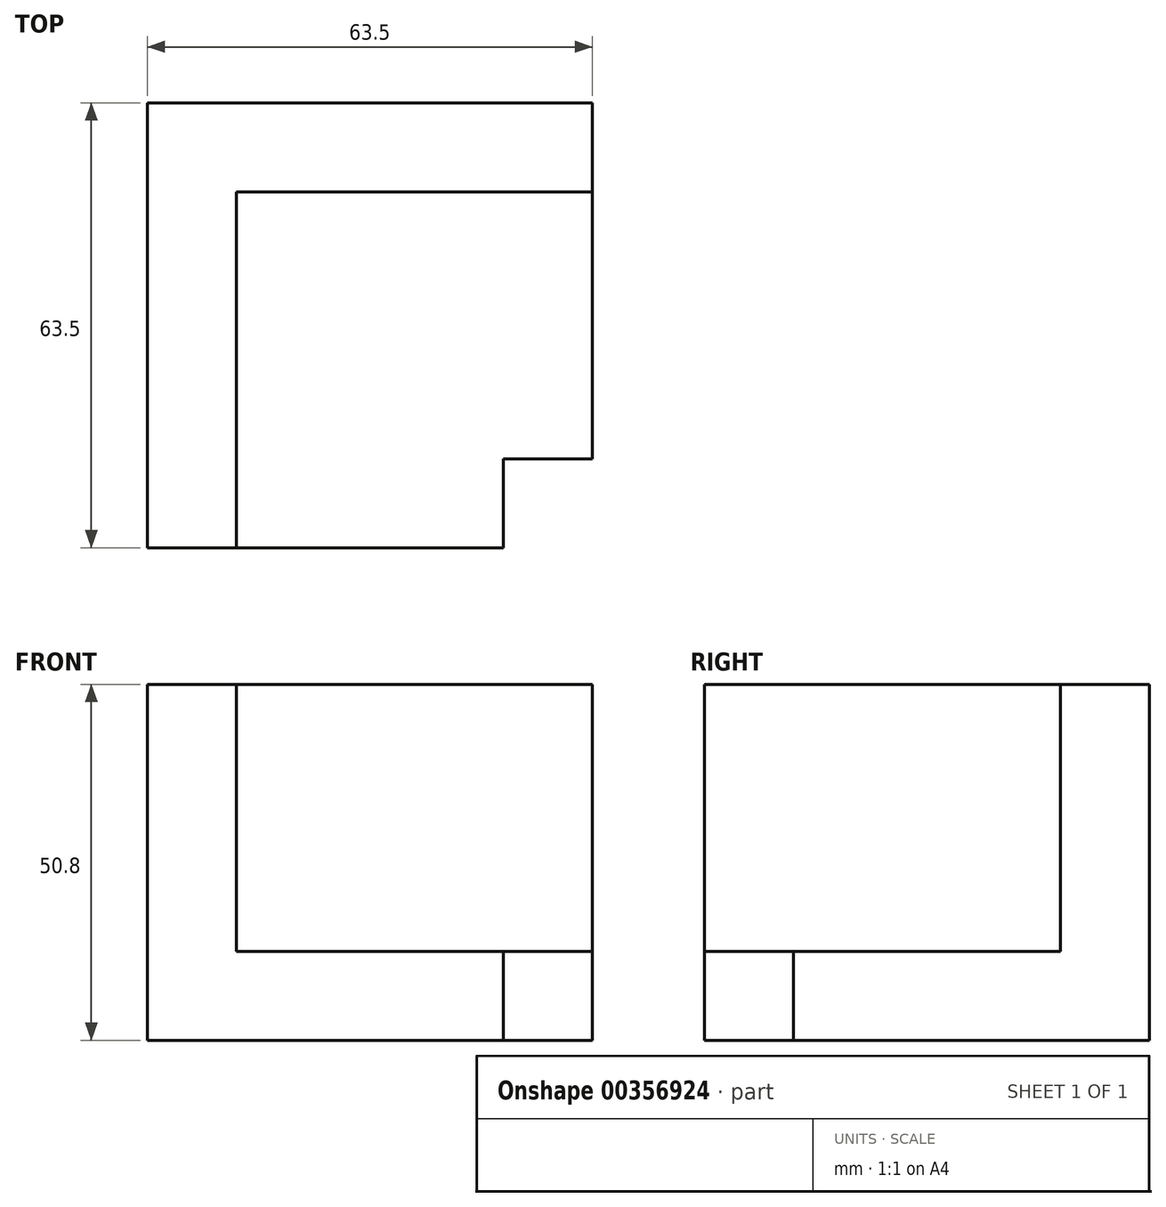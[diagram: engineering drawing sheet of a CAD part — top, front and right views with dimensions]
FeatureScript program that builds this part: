
annotation { "Feature Type Name" : "Feature", "Feature Type Description" : "" }
export const myFeature = defineFeature(function(context is Context, id is Id, definition is map)
    precondition{}
    {
        {
            var Q0;
            Q0=qCreatedBy(makeId("Front.planeOp"),FACE);
            var sketch = newSketch(context, id + "F0", { "sketchPlane" : qUnion([Q0])});
            skLineSegment(sketch, "E0.bottom", {"start": v(0, 0) * mm, "end": v(12.7, 0) * mm});
            skLineSegment(sketch, "E0.top", {"start": v(0, -50.8) * mm, "end": v(12.7, -50.8) * mm});
            skLineSegment(sketch, "E0.left", {"start": v(0, 0) * mm, "end": v(0, -50.8) * mm});
            skLineSegment(sketch, "E0.right", {"start": v(12.7, 0) * mm, "end": v(12.7, -50.8) * mm});
            skSolve(sketch);
        }
        {
            var Q0;
            Q0=makeQuery(id+"F0.imprint","IMPRINT",FACE,{"disambiguationData":[TD([[makeQuery(id+"F0.imprint","IMPRINT",EDGE,{"derivedFrom":sQuery(id+"F0.wireOp",EDGE,"E0.bottom")}),-1.0]])]});
            extrude(context, id + "F1", {"entities" : qUnion([Q0]), "depth" : 63.5 * mm});
        }
        {
            var Q0;
            Q0=makeQuery(id+"F1.opExtrude","SWEPT_FACE",FACE,{"disambiguationData":[OSD([sQuery(id+"F0.wireOp",EDGE,"E0.right")])]});
            var sketch = newSketch(context, id + "F2", { "sketchPlane" : qUnion([Q0])});
            skLineSegment(sketch, "E1.bottom", {"start": v(-63.5, -50.8) * mm, "end": v(0, -50.8) * mm});
            skLineSegment(sketch, "E1.top", {"start": v(-63.5, -38.1) * mm, "end": v(0, -38.1) * mm});
            skLineSegment(sketch, "E1.left", {"start": v(-63.5, -50.8) * mm, "end": v(-63.5, -38.1) * mm});
            skLineSegment(sketch, "E1.right", {"start": v(0, -50.8) * mm, "end": v(0, -38.1) * mm});
            skSolve(sketch);
        }
        {
            var Q0;
            Q0=makeQuery(id+"F2.imprint","IMPRINT",FACE,{"disambiguationData":[TD([[makeQuery(id+"F2.imprint","IMPRINT",EDGE,{"derivedFrom":sQuery(id+"F2.wireOp",EDGE,"E1.bottom")}),1.0]])]});
            extrude(context, id + "F3", {"entities" : qUnion([Q0]), "operationType" : NewBodyOperationType.ADD, "depth" : 50.8 * mm});
        }
        {
            var Q0;
            Q0=makeQuery(id+"F1.opExtrude","SWEPT_FACE",FACE,{"disambiguationData":[OSD([sQuery(id+"F0.wireOp",EDGE,"E0.right")])]});
            var sketch = newSketch(context, id + "F4", { "sketchPlane" : qUnion([Q0])});
            skLineSegment(sketch, "E2.bottom", {"start": v(0, 0) * mm, "end": v(-12.7, 0) * mm});
            skLineSegment(sketch, "E2.top", {"start": v(0, -38.1) * mm, "end": v(-12.7, -38.1) * mm});
            skLineSegment(sketch, "E2.left", {"start": v(0, 0) * mm, "end": v(0, -38.1) * mm});
            skLineSegment(sketch, "E2.right", {"start": v(-12.7, 0) * mm, "end": v(-12.7, -38.1) * mm});
            skSolve(sketch);
        }
        {
            var Q0;
            Q0=makeQuery(id+"F4.imprint","IMPRINT",FACE,{"disambiguationData":[TD([[makeQuery(id+"F4.imprint","IMPRINT",EDGE,{"derivedFrom":sQuery(id+"F4.wireOp",EDGE,"E2.bottom")}),-1.0]])]});
            extrude(context, id + "F5", {"entities" : qUnion([Q0]), "operationType" : NewBodyOperationType.ADD, "depth" : 50.8 * mm});
        }
        {
            var Q0;
            Q0=makeQuery(id+"F5.boolean.opBoolean","MERGE",FACE,{"derivedFrom":[makeQuery(id+"F3.opExtrude","CAP_FACE",FACE,{"disambiguationData":[OSD([sQuery(id+"F2.wireOp",EDGE,"E1.bottom"),sQuery(id+"F2.wireOp",EDGE,"E1.top"),sQuery(id+"F2.wireOp",EDGE,"E1.left"),sQuery(id+"F2.wireOp",EDGE,"E1.right")])],"isStart":false}),makeQuery(id+"F5.opExtrude","CAP_FACE",FACE,{"disambiguationData":[OSD([sQuery(id+"F4.wireOp",EDGE,"E2.bottom"),sQuery(id+"F4.wireOp",EDGE,"E2.top"),sQuery(id+"F4.wireOp",EDGE,"E2.left"),sQuery(id+"F4.wireOp",EDGE,"E2.right")])],"isStart":false})]});
            var sketch = newSketch(context, id + "F6", { "sketchPlane" : qUnion([Q0])});
            skLineSegment(sketch, "E3.bottom", {"start": v(-63.5, -38.1) * mm, "end": v(-50.8, -38.1) * mm});
            skLineSegment(sketch, "E3.top", {"start": v(-63.5, -50.8) * mm, "end": v(-50.8, -50.8) * mm});
            skLineSegment(sketch, "E3.left", {"start": v(-63.5, -38.1) * mm, "end": v(-63.5, -50.8) * mm});
            skLineSegment(sketch, "E3.right", {"start": v(-50.8, -38.1) * mm, "end": v(-50.8, -50.8) * mm});
            skSolve(sketch);
        }
        {
            var Q0;
            Q0=makeQuery(id+"F6.imprint","IMPRINT",FACE,{"disambiguationData":[TD([[makeQuery(id+"F6.imprint","IMPRINT",EDGE,{"derivedFrom":sQuery(id+"F6.wireOp",EDGE,"E3.bottom")}),-1.0]])]});
            extrude(context, id + "F7", {"entities" : qUnion([Q0]), "operationType" : NewBodyOperationType.ADD, "depth" : -12.7 * mm});
        }
        {
            var Q0;
            Q0=makeQuery(id+"F3.opExtrude","SWEPT_FACE",FACE,{"disambiguationData":[OSD([sQuery(id+"F2.wireOp",EDGE,"E1.top")])]});
            var sketch = newSketch(context, id + "F8", { "sketchPlane" : qUnion([Q0])});
            skLineSegment(sketch, "E4.bottom", {"start": v(63.5, -63.5) * mm, "end": v(50.8, -63.5) * mm});
            skLineSegment(sketch, "E4.top", {"start": v(63.5, -50.8) * mm, "end": v(50.8, -50.8) * mm});
            skLineSegment(sketch, "E4.left", {"start": v(63.5, -63.5) * mm, "end": v(63.5, -50.8) * mm});
            skLineSegment(sketch, "E4.right", {"start": v(50.8, -63.5) * mm, "end": v(50.8, -50.8) * mm});
            skSolve(sketch);
        }
        {
            var Q0;
            Q0=makeQuery(id+"F8.imprint","IMPRINT",FACE,{"disambiguationData":[TD([[makeQuery(id+"F8.imprint","IMPRINT",EDGE,{"derivedFrom":sQuery(id+"F8.wireOp",EDGE,"E4.bottom")}),-1.0]])]});
            extrude(context, id + "F9", {"entities" : qUnion([Q0]), "operationType" : NewBodyOperationType.REMOVE, "depth" : -12.7 * mm});
        }
        {
            var Q0;
            Q0=makeQuery(id+"F5.boolean.opBoolean","MERGE",FACE,{"derivedFrom":[makeQuery(id+"F1.opExtrude","SWEPT_FACE",FACE,{"disambiguationData":[OSD([sQuery(id+"F0.wireOp",EDGE,"E0.bottom")])]}),makeQuery(id+"F5.opExtrude","SWEPT_FACE",FACE,{"disambiguationData":[OSD([sQuery(id+"F4.wireOp",EDGE,"E2.bottom")])]})]});
            var sketch = newSketch(context, id + "F10", { "sketchPlane" : qUnion([Q0])});
            skLineSegment(sketch, "E5.bottom", {"start": v(12.7, -63.5) * mm, "end": v(0, -63.5) * mm});
            skLineSegment(sketch, "E5.top", {"start": v(12.7, 0) * mm, "end": v(0, 0) * mm});
            skLineSegment(sketch, "E5.left", {"start": v(12.7, -63.5) * mm, "end": v(12.7, 0) * mm});
            skLineSegment(sketch, "E5.right", {"start": v(0, -63.5) * mm, "end": v(0, 0) * mm});
            skSolve(sketch);
        }
        {
            var Q0;
            Q0 = qSketchRegion(id + "F10", true);
            extrude(context, id + "F11", {"entities" : qUnion([Q0]), "operationType" : NewBodyOperationType.ADD, "depth" : 12.7 * mm});
        }
        {
            var Q0;
            Q0=makeQuery(id+"F5.boolean.opBoolean","MERGE",FACE,{"derivedFrom":[makeQuery(id+"F1.opExtrude","SWEPT_FACE",FACE,{"disambiguationData":[OSD([sQuery(id+"F0.wireOp",EDGE,"E0.bottom")])]}),makeQuery(id+"F5.opExtrude","SWEPT_FACE",FACE,{"disambiguationData":[OSD([sQuery(id+"F4.wireOp",EDGE,"E2.bottom")])]})]});
            var sketch = newSketch(context, id + "F12", { "sketchPlane" : qUnion([Q0])});
            skLineSegment(sketch, "E6.bottom", {"start": v(63.5, -12.7) * mm, "end": v(12.7, -12.7) * mm});
            skLineSegment(sketch, "E6.top", {"start": v(63.5, 0) * mm, "end": v(12.7, 0) * mm});
            skLineSegment(sketch, "E6.left", {"start": v(63.5, -12.7) * mm, "end": v(63.5, 0) * mm});
            skLineSegment(sketch, "E6.right", {"start": v(12.7, -12.7) * mm, "end": v(12.7, 0) * mm});
            skSolve(sketch);
        }
        {
            var Q0;
            Q0 = qSketchRegion(id + "F12", true);
            extrude(context, id + "F13", {"entities" : qUnion([Q0]), "operationType" : NewBodyOperationType.ADD, "depth" : 12.7 * mm});
        }
        {
            var Q0;
            Q0=makeQuery(id+"F11.boolean.opBoolean","MERGE",FACE,{"derivedFrom":[makeQuery(id+"F3.boolean.opBoolean","MERGE",FACE,{"derivedFrom":[makeQuery(id+"F1.opExtrude","CAP_FACE",FACE,{"disambiguationData":[OSD([sQuery(id+"F0.wireOp",EDGE,"E0.bottom"),sQuery(id+"F0.wireOp",EDGE,"E0.top"),sQuery(id+"F0.wireOp",EDGE,"E0.left"),sQuery(id+"F0.wireOp",EDGE,"E0.right")])],"isStart":false}),makeQuery(id+"F3.opExtrude","SWEPT_FACE",FACE,{"disambiguationData":[OSD([sQuery(id+"F2.wireOp",EDGE,"E1.left")])]})]}),makeQuery(id+"F11.opExtrude","SWEPT_FACE",FACE,{"disambiguationData":[OSD([sQuery(id+"F10.wireOp",EDGE,"E5.bottom")])]})]});
            var sketch = newSketch(context, id + "F14", { "sketchPlane" : qUnion([Q0])});
            skLineSegment(sketch, "E7.bottom", {"start": v(50.8, -38.1) * mm, "end": v(0, -38.1) * mm});
            skLineSegment(sketch, "E7.top", {"start": v(50.8, -50.8) * mm, "end": v(0, -50.8) * mm});
            skLineSegment(sketch, "E7.left", {"start": v(50.8, -38.1) * mm, "end": v(50.8, -50.8) * mm});
            skLineSegment(sketch, "E7.right", {"start": v(0, -38.1) * mm, "end": v(0, -50.8) * mm});
            skLineSegment(sketch, "E8.bottom", {"start": v(12.7, 12.7) * mm, "end": v(0, 12.7) * mm});
            skLineSegment(sketch, "E8.top", {"start": v(12.7, -38.1) * mm, "end": v(0, -38.1) * mm});
            skLineSegment(sketch, "E8.left", {"start": v(12.7, 12.7) * mm, "end": v(12.7, -38.1) * mm});
            skLineSegment(sketch, "E8.right", {"start": v(0, 12.7) * mm, "end": v(0, -38.1) * mm});
            skSolve(sketch);
        }
        {
            var Q0;
            Q0 = qSketchRegion(id + "F14", true);
            extrude(context, id + "F15", {"entities" : qUnion([Q0]), "operationType" : NewBodyOperationType.ADD, "depth" : 12.7 * mm});
        }
        {
            var Q0;
            Q0=makeQuery(id+"F13.boolean.opBoolean","MERGE",FACE,{"derivedFrom":[makeQuery(id+"F5.boolean.opBoolean","MERGE",FACE,{"derivedFrom":[makeQuery(id+"F3.opExtrude","CAP_FACE",FACE,{"disambiguationData":[OSD([sQuery(id+"F2.wireOp",EDGE,"E1.bottom"),sQuery(id+"F2.wireOp",EDGE,"E1.top"),sQuery(id+"F2.wireOp",EDGE,"E1.left"),sQuery(id+"F2.wireOp",EDGE,"E1.right")])],"isStart":false}),makeQuery(id+"F5.opExtrude","CAP_FACE",FACE,{"disambiguationData":[OSD([sQuery(id+"F4.wireOp",EDGE,"E2.bottom"),sQuery(id+"F4.wireOp",EDGE,"E2.top"),sQuery(id+"F4.wireOp",EDGE,"E2.left"),sQuery(id+"F4.wireOp",EDGE,"E2.right")])],"isStart":false})]}),makeQuery(id+"F13.opExtrude","SWEPT_FACE",FACE,{"disambiguationData":[OSD([sQuery(id+"F12.wireOp",EDGE,"E6.left")])]})]});
            var sketch = newSketch(context, id + "F16", { "sketchPlane" : qUnion([Q0])});
            skLineSegment(sketch, "E9.bottom", {"start": v(-50.8, -50.8) * mm, "end": v(0, -50.8) * mm});
            skLineSegment(sketch, "E9.top", {"start": v(-50.8, -38.1) * mm, "end": v(0, -38.1) * mm});
            skLineSegment(sketch, "E9.left", {"start": v(-50.8, -50.8) * mm, "end": v(-50.8, -38.1) * mm});
            skLineSegment(sketch, "E9.right", {"start": v(0, -50.8) * mm, "end": v(0, -38.1) * mm});
            skLineSegment(sketch, "E10.bottom", {"start": v(-12.7, 12.7) * mm, "end": v(0, 12.7) * mm});
            skLineSegment(sketch, "E10.top", {"start": v(-12.7, -38.1) * mm, "end": v(0, -38.1) * mm});
            skLineSegment(sketch, "E10.left", {"start": v(-12.7, 12.7) * mm, "end": v(-12.7, -38.1) * mm});
            skLineSegment(sketch, "E10.right", {"start": v(0, 12.7) * mm, "end": v(0, -38.1) * mm});
            skSolve(sketch);
        }
        {
            var Q0;
            Q0 = qSketchRegion(id + "F16", true);
            extrude(context, id + "F17", {"entities" : qUnion([Q0]), "operationType" : NewBodyOperationType.ADD, "depth" : 12.7 * mm});
        }
        {
            var Q0;
            Q0=makeQuery(id+"F15.boolean.opBoolean","MERGE",FACE,{"derivedFrom":[makeQuery(id+"F9.boolean.opBoolean","COPY",FACE,{"derivedFrom":makeQuery(id+"F9.opExtrude","SWEPT_FACE",FACE,{"disambiguationData":[OSD([sQuery(id+"F8.wireOp",EDGE,"E4.right")])]})}),makeQuery(id+"F15.opExtrude","SWEPT_FACE",FACE,{"disambiguationData":[OSD([sQuery(id+"F14.wireOp",EDGE,"E7.left")])]})]});
            var sketch = newSketch(context, id + "F18", { "sketchPlane" : qUnion([Q0])});
            skLineSegment(sketch, "E11.bottom", {"start": v(-50.8, -38.1) * mm, "end": v(-63.5, -38.1) * mm});
            skLineSegment(sketch, "E11.top", {"start": v(-50.8, -50.8) * mm, "end": v(-63.5, -50.8) * mm});
            skLineSegment(sketch, "E11.left", {"start": v(-50.8, -38.1) * mm, "end": v(-50.8, -50.8) * mm});
            skLineSegment(sketch, "E11.right", {"start": v(-63.5, -38.1) * mm, "end": v(-63.5, -50.8) * mm});
            skSolve(sketch);
        }
        {
            var Q0;
            Q0 = qSketchRegion(id + "F18", true);
            extrude(context, id + "F19", {"entities" : qUnion([Q0]), "operationType" : NewBodyOperationType.ADD, "depth" : 25.4 * mm});
        }
        {
            var Q0;
            Q0=makeQuery(id+"F15.boolean.opBoolean","MERGE",FACE,{"derivedFrom":[makeQuery(id+"F9.boolean.opBoolean","COPY",FACE,{"derivedFrom":makeQuery(id+"F9.opExtrude","SWEPT_FACE",FACE,{"disambiguationData":[OSD([sQuery(id+"F8.wireOp",EDGE,"E4.right")])]})}),makeQuery(id+"F15.opExtrude","SWEPT_FACE",FACE,{"disambiguationData":[OSD([sQuery(id+"F14.wireOp",EDGE,"E7.left")])]})]});
            var sketch = newSketch(context, id + "F20", { "sketchPlane" : qUnion([Q0])});
            skLineSegment(sketch, "E12.bottom", {"start": v(-76.2, -38.1) * mm, "end": v(-63.5, -38.1) * mm});
            skLineSegment(sketch, "E12.top", {"start": v(-76.2, -50.8) * mm, "end": v(-63.5, -50.8) * mm});
            skLineSegment(sketch, "E12.left", {"start": v(-76.2, -38.1) * mm, "end": v(-76.2, -50.8) * mm});
            skLineSegment(sketch, "E12.right", {"start": v(-63.5, -38.1) * mm, "end": v(-63.5, -50.8) * mm});
            skSolve(sketch);
        }
        {
            var Q0;
            Q0 = qSketchRegion(id + "F20", true);
            extrude(context, id + "F21", {"entities" : qUnion([Q0]), "operationType" : NewBodyOperationType.ADD, "depth" : 12.7 * mm});
        }
        {
            var Q0;
            Q0=makeQuery(id+"F17.boolean.opBoolean","MERGE",FACE,{"derivedFrom":[makeQuery(id+"F15.boolean.opBoolean","MERGE",FACE,{"derivedFrom":[makeQuery(id+"F13.boolean.opBoolean","MERGE",FACE,{"derivedFrom":[makeQuery(id+"F11.opExtrude","CAP_FACE",FACE,{"disambiguationData":[OSD([sQuery(id+"F10.wireOp",EDGE,"E5.bottom"),sQuery(id+"F10.wireOp",EDGE,"E5.top"),sQuery(id+"F10.wireOp",EDGE,"E5.left"),sQuery(id+"F10.wireOp",EDGE,"E5.right")])],"isStart":false}),makeQuery(id+"F13.opExtrude","CAP_FACE",FACE,{"disambiguationData":[OSD([sQuery(id+"F12.wireOp",EDGE,"E6.bottom"),sQuery(id+"F12.wireOp",EDGE,"E6.top"),sQuery(id+"F12.wireOp",EDGE,"E6.left"),sQuery(id+"F12.wireOp",EDGE,"E6.right")])],"isStart":false})]}),makeQuery(id+"F15.opExtrude","SWEPT_FACE",FACE,{"disambiguationData":[OSD([sQuery(id+"F14.wireOp",EDGE,"E8.bottom")])]})]}),makeQuery(id+"F17.opExtrude","SWEPT_FACE",FACE,{"disambiguationData":[OSD([sQuery(id+"F16.wireOp",EDGE,"E10.bottom")])]})]});
            var sketch = newSketch(context, id + "F22", { "sketchPlane" : qUnion([Q0])});
            skLineSegment(sketch, "E13.bottom", {"start": v(76.2, 0) * mm, "end": v(0, 0) * mm});
            skLineSegment(sketch, "E13.top", {"start": v(76.2, -12.7) * mm, "end": v(0, -12.7) * mm});
            skLineSegment(sketch, "E13.left", {"start": v(76.2, 0) * mm, "end": v(76.2, -12.7) * mm});
            skLineSegment(sketch, "E13.right", {"start": v(0, 0) * mm, "end": v(0, -12.7) * mm});
            skLineSegment(sketch, "E14.bottom", {"start": v(0, -12.7) * mm, "end": v(12.7, -12.7) * mm});
            skLineSegment(sketch, "E14.top", {"start": v(0, -76.2) * mm, "end": v(12.7, -76.2) * mm});
            skLineSegment(sketch, "E14.left", {"start": v(0, -12.7) * mm, "end": v(0, -76.2) * mm});
            skLineSegment(sketch, "E14.right", {"start": v(12.7, -12.7) * mm, "end": v(12.7, -76.2) * mm});
            skSolve(sketch);
        }
        {
            var Q0;
            Q0 = qSketchRegion(id + "F22", true);
            extrude(context, id + "F23", {"entities" : qUnion([Q0]), "operationType" : NewBodyOperationType.REMOVE, "oppositeDirection" : true, "depth" : 12.7 * mm});
        }
        {
            var Q0;
            Q0=makeQuery(id+"F19.boolean.opBoolean","MERGE",FACE,{"derivedFrom":[makeQuery(id+"F17.opExtrude","CAP_FACE",FACE,{"disambiguationData":[OSD([sQuery(id+"F16.wireOp",EDGE,"E9.bottom"),sQuery(id+"F16.wireOp",EDGE,"E9.top"),sQuery(id+"F16.wireOp",EDGE,"E9.left"),sQuery(id+"F16.wireOp",EDGE,"E9.right"),sQuery(id+"F16.wireOp",EDGE,"E10.bottom"),sQuery(id+"F16.wireOp",EDGE,"E10.left"),sQuery(id+"F16.wireOp",EDGE,"E10.right")])],"isStart":false}),makeQuery(id+"F19.opExtrude","CAP_FACE",FACE,{"disambiguationData":[OSD([sQuery(id+"F18.wireOp",EDGE,"E11.bottom"),sQuery(id+"F18.wireOp",EDGE,"E11.top"),sQuery(id+"F18.wireOp",EDGE,"E11.left"),sQuery(id+"F18.wireOp",EDGE,"E11.right")])],"isStart":false})]});
            var sketch = newSketch(context, id + "F24", { "sketchPlane" : qUnion([Q0])});
            skPoint(sketch, "E15.oppositeSnap0", {"position": v(-38.1, -38.1) * mm});
            skLineSegment(sketch, "E15.bottom", {"start": v(-63.5, -50.8) * mm, "end": v(0, -50.8) * mm});
            skLineSegment(sketch, "E15.top", {"start": v(-63.5, -38.1) * mm, "end": v(0, -38.1) * mm});
            skLineSegment(sketch, "E15.left", {"start": v(-63.5, -50.8) * mm, "end": v(-63.5, -38.1) * mm});
            skLineSegment(sketch, "E15.right", {"start": v(0, -50.8) * mm, "end": v(0, -38.1) * mm});
            skLineSegment(sketch, "E16.bottom", {"start": v(0, 0) * mm, "end": v(-12.7, 0) * mm});
            skLineSegment(sketch, "E16.top", {"start": v(0, -38.1) * mm, "end": v(-12.7, -38.1) * mm});
            skLineSegment(sketch, "E16.left", {"start": v(0, 0) * mm, "end": v(0, -38.1) * mm});
            skLineSegment(sketch, "E16.right", {"start": v(-12.7, 0) * mm, "end": v(-12.7, -38.1) * mm});
            skSolve(sketch);
        }
        {
            var Q0;
            Q0 = qSketchRegion(id + "F24", true);
            extrude(context, id + "F25", {"entities" : qUnion([Q0]), "operationType" : NewBodyOperationType.REMOVE, "oppositeDirection" : true, "depth" : 12.7 * mm});
        }
        {
            var Q0;
            Q0=makeQuery(id+"F21.boolean.opBoolean","MERGE",FACE,{"derivedFrom":[makeQuery(id+"F15.opExtrude","CAP_FACE",FACE,{"disambiguationData":[OSD([sQuery(id+"F14.wireOp",EDGE,"E7.bottom"),sQuery(id+"F14.wireOp",EDGE,"E7.top"),sQuery(id+"F14.wireOp",EDGE,"E7.left"),sQuery(id+"F14.wireOp",EDGE,"E7.right"),sQuery(id+"F14.wireOp",EDGE,"E8.bottom"),sQuery(id+"F14.wireOp",EDGE,"E8.left"),sQuery(id+"F14.wireOp",EDGE,"E8.right")])],"isStart":false}),makeQuery(id+"F21.opExtrude","SWEPT_FACE",FACE,{"disambiguationData":[OSD([sQuery(id+"F20.wireOp",EDGE,"E12.left")])]})]});
            var sketch = newSketch(context, id + "F26", { "sketchPlane" : qUnion([Q0])});
            skLineSegment(sketch, "E17.bottom", {"start": v(63.5, -38.1) * mm, "end": v(0, -38.1) * mm});
            skLineSegment(sketch, "E17.top", {"start": v(63.5, -50.8) * mm, "end": v(0, -50.8) * mm});
            skLineSegment(sketch, "E17.left", {"start": v(63.5, -38.1) * mm, "end": v(63.5, -50.8) * mm});
            skLineSegment(sketch, "E17.right", {"start": v(0, -38.1) * mm, "end": v(0, -50.8) * mm});
            skLineSegment(sketch, "E18.bottom", {"start": v(0, 0) * mm, "end": v(12.7, 0) * mm});
            skLineSegment(sketch, "E18.top", {"start": v(0, -38.1) * mm, "end": v(12.7, -38.1) * mm});
            skLineSegment(sketch, "E18.left", {"start": v(0, 0) * mm, "end": v(0, -38.1) * mm});
            skLineSegment(sketch, "E18.right", {"start": v(12.7, 0) * mm, "end": v(12.7, -38.1) * mm});
            skSolve(sketch);
        }
        {
            var Q0;
            Q0 = qSketchRegion(id + "F26", true);
            extrude(context, id + "F27", {"entities" : qUnion([Q0]), "operationType" : NewBodyOperationType.REMOVE, "oppositeDirection" : true, "depth" : 12.7 * mm});
        }
        {
            var Q0;
            Q0=makeQuery(id+"F25.boolean.opBoolean","MERGE",FACE,{"derivedFrom":[makeQuery(id+"F21.opExtrude","CAP_FACE",FACE,{"disambiguationData":[OSD([sQuery(id+"F20.wireOp",EDGE,"E12.bottom"),sQuery(id+"F20.wireOp",EDGE,"E12.top"),sQuery(id+"F20.wireOp",EDGE,"E12.left"),sQuery(id+"F20.wireOp",EDGE,"E12.right")])],"isStart":false}),makeQuery(id+"F25.opExtrude","CAP_FACE",FACE,{"disambiguationData":[OSD([sQuery(id+"F24.wireOp",EDGE,"E15.bottom"),sQuery(id+"F24.wireOp",EDGE,"E15.top"),sQuery(id+"F24.wireOp",EDGE,"E15.left"),sQuery(id+"F24.wireOp",EDGE,"E15.right"),sQuery(id+"F24.wireOp",EDGE,"E16.bottom"),sQuery(id+"F24.wireOp",EDGE,"E16.left"),sQuery(id+"F24.wireOp",EDGE,"E16.right")])],"isStart":false})]});
            var sketch = newSketch(context, id + "F28", { "sketchPlane" : qUnion([Q0])});
            skLineSegment(sketch, "E19.bottom", {"start": v(-63.5, -38.1) * mm, "end": v(-50.8, -38.1) * mm});
            skLineSegment(sketch, "E19.top", {"start": v(-63.5, -50.8) * mm, "end": v(-50.8, -50.8) * mm});
            skLineSegment(sketch, "E19.left", {"start": v(-63.5, -38.1) * mm, "end": v(-63.5, -50.8) * mm});
            skLineSegment(sketch, "E19.right", {"start": v(-50.8, -38.1) * mm, "end": v(-50.8, -50.8) * mm});
            skSolve(sketch);
        }
        {
            var Q0;
            Q0=makeQuery(id+"F28.imprint","IMPRINT",FACE,{"disambiguationData":[TD([[makeQuery(id+"F28.imprint","IMPRINT",EDGE,{"derivedFrom":sQuery(id+"F28.wireOp",EDGE,"E19.bottom")}),-1.0]])]});
            extrude(context, id + "F29", {"entities" : qUnion([Q0]), "operationType" : NewBodyOperationType.REMOVE, "oppositeDirection" : true, "depth" : 12.7 * mm});
        }
    });
